# Revit family: Faucet-Deck_Mount-Bath_Shower-KOHLER-FINIAL-K-8793T
name_source: partatom
category: Plumbing Fixtures
revit_build: Autodesk Revit 2017 (Build: 20160225_1515(x64)
units: mm (PartAtom-declared; Revit-internal decimal feet)

## family parameters
Cut with Voids When Loaded = No
Host = Face
OmniClass Number = 23.31.11.00
OmniClass Title = Faucets
Part Type = Normal
Room Calculation Point = No
Round Connector Dimension = Use Diameter
Shared = No

## types (5) — shared parameters
ADA Compliant = No
Assembly Code = D2010
CW Connection = Yes
Cold Water Inlet = Cold Water Inlet
Date Modified = 09/07/2020
Default Elevation = 36"
Drain Included = No
Faucet Hole Spacing = 8 1/16"
Flow Rate = 0 GPM
HW Connection = Yes
Handle Clearance = 3 13/16"
Height = 10 15/16"
Hot Water Inlet = Hot Water Inlet
Length = 12"
Manufacturer = KOHLER Co.
Master Format 2014 = 22 41 39
Master Format 2014 Name = Residential Faucets, Supplies, and Trim
Material = Premium Metal Construction
Pressure = 0.00 psi
Product Documentation Link = https://files.kohler.com.cn
Product Name = FINIAL
Spout Reach = 12"
URL = http://www.kohler.com.cn
Vent Connection = No
Waste Connection = No
Waste Water Outlet = Waste Water Outlet
WaterSense Certified = No
Width = 8 1/16"

## per-type parameters (varying)
| type | Ceramic Handle | Description | Finish | Handle Finish | Model | Product Page URL | Type |
| Metal Handle, CP-Polished Chrome | No | Floor-standing bathtub shower faucet classic handle | Kohler-Metal-CP-Polished_Chrome | Kohler-Metal-CP-Polished_Chrome | K-8793T-4M-CP | https://www.kohler.com.cn | 1 |
| Metal Handle, AF-Flange Gold | No | Floor-standing bathtub shower faucet classic handle | Kohler-Metal-AF-Flange_Gold | Kohler-Metal-AF-Flange_Gold | K-8793T-4M-AF | https://www.kohler.com.cn | 2 |
| Metal Handle, SN-Champagne Gold | No | Floor-standing bathtub shower faucet classic handle | Kohler-Metal-SN-Champagne_Gold | Kohler-Metal-SN-Champagne_Gold | K-8793T-4M-SN | https://www.kohler.com.cn | 3 |
| Metal Handle, R2B-Black Yaojin | No | Floor-standing bathtub shower faucet classic handle | Kohler-Metal-BL-Matte_Black | Kohler-Metal-RGD-Rose_Gold | K-8793T-4M-R2B | https://www.kohler.com.cn | 4 |
| Ceramic Handle, CP-Polished Chrome | Yes | Floor Mount bath Shower Faucet, with Bracke | Kohler-Metal-CP-Polished_Chrome | Kohler-Metal-CP-Polished_Chrome | K-8793T-4P-CP |  | 5 |

## geometry (parser evidence)
native form markers: Sweep x6
no freeform markers — native parametric forms only
